# Revit family: Thorn AQUAFORCE PRO
name_source: partatom
category: Leuchten
revit_build: Autodesk Revit 2016 (Build: 20150714_1515(x64)
units: mm (PartAtom-declared; Revit-internal decimal feet)

## family parameters
Basisbauteil = Fläche
Beim Laden mit Abzugskörper schneiden = Nein
Bemaßung runder Anschluss = Durchmesser verwenden
Gemeinsam genutzt = Nein
Lichtquelle = Ja
OmniClass-Nummer = 23.80.70.11
OmniClass-Titel = Luminaries for Internal Lighting
Raumberechnungspunkt = Nein
Teiletyp = Normal

## types (8) — shared parameters
Baugruppenkennzeichen = D5020210
Beschreibung = Moisture-proof diffuser luminaire
Body = Thorn_Metal_Light_Grey
Cover = Thorn_PMMA_Semitransparent_SI
Emissionsform beim Rendern sichtbar = Nein
Farbfilter = 16777215
Farbtemperaturverschiebung bei Dämpfen der Lampe = <Keine Auswahl>
Height = 92 mm  [stored 0.301837 ft]
Hersteller = Thorn Lighting
Lampe = LED
Neigungswinkel = -90.00°
Voltage = 230 V
Von Länge des Rechtecks aussenden = 90 mm  [stored 0.295276 ft]
Width = 90 mm  [stored 0.295276 ft]
zero-valued in all types: Vorgabe-Ansicht

## per-type parameters (varying)
| type | Datei für fotometrisches Netz | Length | Modell | Scheinlast | URL | Von Breite des Rechtecks ausssenden |
| AQFPRO L 4300 WB | D39803AA_AQFPRO_L_LED4300-840_PC_WB_HF.IES | 1600 mm  [stored 5.24934 ft] | 96630756 | 33 VA | www.thornlighting.com/96630756 | 1600 mm  [stored 5.24934 ft] |
| AQFPRO L 6400 MB | D39801AA_AQFPRO_L_LED6400-840_PC_MB_HF.IES | 1600 mm  [stored 5.24934 ft] | 96630757 | 50 VA | www.thornlighting.com/96630757 | 1600 mm  [stored 5.24934 ft] |
| AQFPRO L 8000 MB | D39801AA_AQFPRO_L_LED8000-840_PC_MB_HF.IES | 1600 mm  [stored 5.24934 ft] | 96630758 | 62 VA | www.thornlighting.com/96630758 | 1600 mm  [stored 5.24934 ft] |
| AQFPRO S 2900 MB | D39801AA_AQFPRO_S_LED2900-840_PC_MB_HF.IES | 1100 mm | 96630753 | 21 VA | www.thornlighting.com/96630753 | 1100 mm |
| AQFPRO S 4300 MB | D39801AA_AQFPRO_S_LED4300-840_PC_MB_HF.IES | 1100 mm | 96630754 | 33 VA | www.thornlighting.com/96630754 | 1100 mm |
| AQFPRO S 5200 MB | D39801AA_AQFPRO_S_LED5200-840_PC_MB_HF.IES | 1100 mm | 96630755 | 42 VA | www.thornlighting.com/96630755 | 1100 mm |
| AQFPRO S 2900 WB | 92901967-D39803AA_AQFPRO_S_LED2900-840_PC_WB_HF.IES | 1100 mm | 92901967 | 22 VA | www.thornlighting.com/92901967 | 1100 mm |
| AQFPRO S 5200 WB | 92901935-D39803AA_AQFPRO_S_LED5200-840_PC_WB_HF.IES | 1100 mm | 92901935 | 43 VA | www.thornlighting.com/92901935 | 1100 mm |

note: [stored X ft] marks values corroborated as IEEE doubles in the binary element streams (Revit-internal decimal feet)

## geometry (parser evidence)
native form markers: Blend x2, Sweep x4
no freeform markers — native parametric forms only
